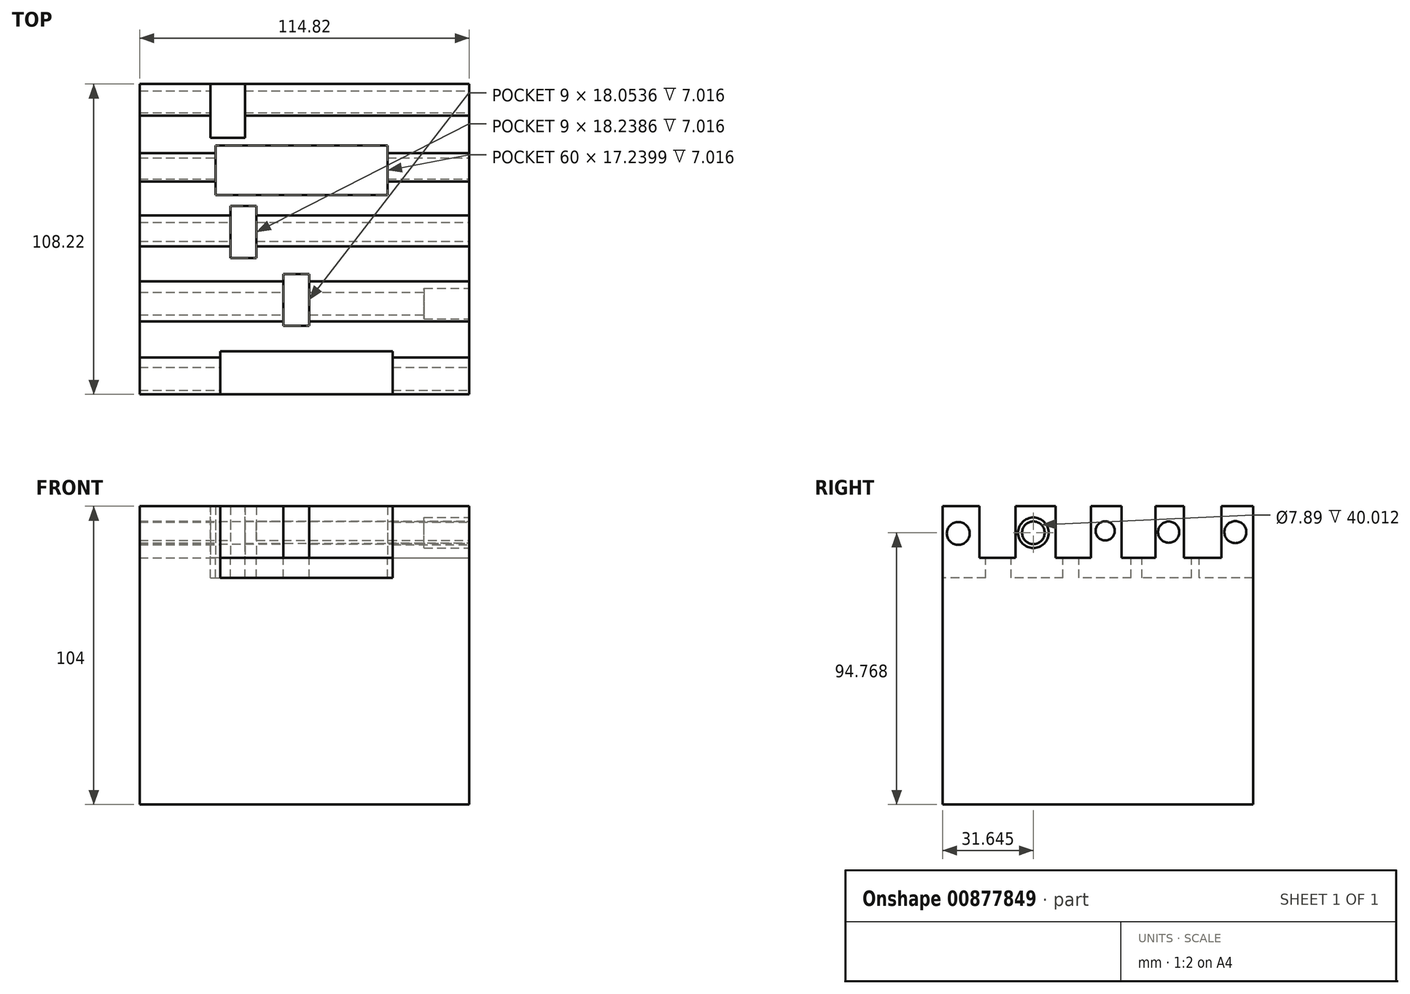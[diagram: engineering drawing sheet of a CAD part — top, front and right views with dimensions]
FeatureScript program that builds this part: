
annotation { "Feature Type Name" : "Feature", "Feature Type Description" : "" }
export const myFeature = defineFeature(function(context is Context, id is Id, definition is map)
    precondition{}
    {
        {
            var Q0;
            Q0=qCreatedBy(makeId("Top.planeOp"),FACE);
            var sketch = newSketch(context, id + "F0", { "sketchPlane" : qUnion([Q0])});
            skLineSegment(sketch, "E0.bottom", {"start": v(-43.96, -51.67) * mm, "end": v(70.86, -51.67) * mm});
            skLineSegment(sketch, "E0.top", {"start": v(-43.96, 56.55) * mm, "end": v(70.86, 56.55) * mm});
            skLineSegment(sketch, "E0.left", {"start": v(-43.96, -51.67) * mm, "end": v(-43.96, 56.55) * mm});
            skLineSegment(sketch, "E0.right", {"start": v(70.86, -51.67) * mm, "end": v(70.86, 56.55) * mm});
            skSolve(sketch);
        }
        {
            var Q0;
            Q0 = qSketchRegion(id + "F0", true);
            extrude(context, id + "F1", {"entities" : qUnion([Q0]), "depth" : 104 * mm, "offsetDistance" : 25 * mm});
        }
        {
            var Q0;
            Q0=makeQuery(id+"F1.opExtrude","SWEPT_FACE",FACE,{"disambiguationData":[OSD([sQuery(id+"F0.wireOp",EDGE,"E0.right")])]});
            var sketch = newSketch(context, id + "F2", { "sketchPlane" : qUnion([Q0])});
            skLineSegment(sketch, "E1.bottom", {"start": v(-38.8, 106.76) * mm, "end": v(-26.27, 106.76) * mm});
            skLineSegment(sketch, "E1.top", {"start": v(-38.8, 86.02) * mm, "end": v(-26.27, 86.02) * mm});
            skLineSegment(sketch, "E1.left", {"start": v(-38.8, 106.76) * mm, "end": v(-38.8, 86.02) * mm});
            skLineSegment(sketch, "E1.right", {"start": v(-26.27, 106.76) * mm, "end": v(-26.27, 86.02) * mm});
            skLineSegment(sketch, "E2.bottom", {"start": v(-12.25, 106.58) * mm, "end": v(0, 106.58) * mm});
            skLineSegment(sketch, "E2.top", {"start": v(-12.25, 86.02) * mm, "end": v(0, 86.02) * mm});
            skLineSegment(sketch, "E2.left", {"start": v(-12.25, 106.58) * mm, "end": v(-12.25, 86.02) * mm});
            skLineSegment(sketch, "E2.right", {"start": v(0, 106.58) * mm, "end": v(0, 86.02) * mm});
            skLineSegment(sketch, "E3.bottom", {"start": v(10.74, 106.76) * mm, "end": v(22.52, 106.76) * mm});
            skLineSegment(sketch, "E3.top", {"start": v(10.74, 86.02) * mm, "end": v(22.52, 86.02) * mm});
            skLineSegment(sketch, "E3.left", {"start": v(10.74, 106.76) * mm, "end": v(10.74, 86.02) * mm});
            skLineSegment(sketch, "E3.right", {"start": v(22.52, 106.76) * mm, "end": v(22.52, 86.02) * mm});
            skLineSegment(sketch, "E4.bottom", {"start": v(32.43, 106.58) * mm, "end": v(45.51, 106.58) * mm});
            skLineSegment(sketch, "E4.top", {"start": v(32.43, 86.02) * mm, "end": v(45.51, 86.02) * mm});
            skLineSegment(sketch, "E4.left", {"start": v(32.43, 106.58) * mm, "end": v(32.43, 86.02) * mm});
            skLineSegment(sketch, "E4.right", {"start": v(45.51, 106.58) * mm, "end": v(45.51, 86.02) * mm});
            skSolve(sketch);
        }
        {
            var Q0;
            Q0 = qSketchRegion(id + "F2", true);
            extrude(context, id + "F3", {"entities" : qUnion([Q0]), "operationType" : NewBodyOperationType.REMOVE, "endBound" : BoundingType.THROUGH_ALL, "oppositeDirection" : true, "depth" : 25 * mm, "offsetDistance" : 25 * mm});
        }
        {
            var Q0;
            {var subQ0=sQuery(id+"F0.wireOp",EDGE,"E0.bottom");var subQ1=sQuery(id+"F0.wireOp",EDGE,"E0.right");var subQ2=sQuery(id+"F0.wireOp",EDGE,"E0.left");Q0=makeQuery(id+"F3.boolean.opBoolean","SPLIT",FACE,{"disambiguationData":[TD([makeQuery(id+"F1.opExtrude","SWEPT_FACE",FACE,{"disambiguationData":[OSD([subQ0])]})])],"derivedFrom":makeQuery(id+"F1.opExtrude","CAP_FACE",FACE,{"disambiguationData":[OSD([subQ0,sQuery(id+"F0.wireOp",EDGE,"E0.top"),subQ2,subQ1])],"isStart":false})});}
            var sketch = newSketch(context, id + "F4", { "sketchPlane" : qUnion([Q0])});
            skLineSegment(sketch, "E5.bottom", {"start": v(-15.85, -36.65) * mm, "end": v(44.15, -36.65) * mm});
            skLineSegment(sketch, "E5.top", {"start": v(-15.85, -53.69) * mm, "end": v(44.15, -53.69) * mm});
            skLineSegment(sketch, "E5.left", {"start": v(-15.85, -36.65) * mm, "end": v(-15.85, -53.69) * mm});
            skLineSegment(sketch, "E5.right", {"start": v(44.15, -36.65) * mm, "end": v(44.15, -53.69) * mm});
            skLineSegment(sketch, "E6.bottom", {"start": v(6.15, -9.7) * mm, "end": v(15.15, -9.7) * mm});
            skLineSegment(sketch, "E6.top", {"start": v(6.15, -27.75) * mm, "end": v(15.15, -27.75) * mm});
            skLineSegment(sketch, "E6.left", {"start": v(6.15, -9.7) * mm, "end": v(6.15, -27.75) * mm});
            skLineSegment(sketch, "E6.right", {"start": v(15.15, -9.7) * mm, "end": v(15.15, -27.75) * mm});
            skLineSegment(sketch, "E7.bottom", {"start": v(-12.27, 14.08) * mm, "end": v(-3.27, 14.08) * mm});
            skLineSegment(sketch, "E7.top", {"start": v(-12.27, -4.16) * mm, "end": v(-3.27, -4.16) * mm});
            skLineSegment(sketch, "E7.left", {"start": v(-12.27, 14.08) * mm, "end": v(-12.27, -4.16) * mm});
            skLineSegment(sketch, "E7.right", {"start": v(-3.27, 14.08) * mm, "end": v(-3.27, -4.16) * mm});
            skLineSegment(sketch, "E8.bottom", {"start": v(-17.55, 35.07) * mm, "end": v(42.45, 35.07) * mm});
            skLineSegment(sketch, "E8.top", {"start": v(-17.55, 17.83) * mm, "end": v(42.45, 17.83) * mm});
            skLineSegment(sketch, "E8.left", {"start": v(-17.55, 35.07) * mm, "end": v(-17.55, 17.83) * mm});
            skLineSegment(sketch, "E8.right", {"start": v(42.45, 35.07) * mm, "end": v(42.45, 17.83) * mm});
            skLineSegment(sketch, "E9.bottom", {"start": v(-19.26, 60.98) * mm, "end": v(-7.26, 60.98) * mm});
            skLineSegment(sketch, "E9.top", {"start": v(-19.26, 37.77) * mm, "end": v(-7.26, 37.77) * mm});
            skLineSegment(sketch, "E9.left", {"start": v(-19.26, 60.98) * mm, "end": v(-19.26, 37.77) * mm});
            skLineSegment(sketch, "E9.right", {"start": v(-7.26, 60.98) * mm, "end": v(-7.26, 37.77) * mm});
            skSolve(sketch);
        }
        {
            var Q0;
            Q0 = qSketchRegion(id + "F4", true);
            var Q1;
            {var subQ0=sQuery(id+"F0.wireOp",EDGE,"E0.left");var subQ1=sQuery(id+"F0.wireOp",EDGE,"E0.right");Q1=makeQuery(id+"F3.boolean.opBoolean","SPLIT",FACE,{"disambiguationData":[TD([makeQuery(id+"F3.opExtrude","SWEPT_FACE",FACE,{"disambiguationData":[OSD([sQuery(id+"F2.wireOp",EDGE,"E3.right")])]})])],"derivedFrom":makeQuery(id+"F1.opExtrude","CAP_FACE",FACE,{"disambiguationData":[OSD([sQuery(id+"F0.wireOp",EDGE,"E0.bottom"),sQuery(id+"F0.wireOp",EDGE,"E0.top"),subQ0,subQ1])],"isStart":false})});}
            extrude(context, id + "F5", {"entities" : qUnion([Q0]), "operationType" : NewBodyOperationType.REMOVE, "oppositeDirection" : true, "depth" : 25 * mm, "endBoundEntityFace" : qUnion([Q1]), "offsetDistance" : 25 * mm});
        }
        {
            var Q0;
            Q0=makeQuery(id+"F1.opExtrude","SWEPT_FACE",FACE,{"disambiguationData":[OSD([sQuery(id+"F0.wireOp",EDGE,"E0.right")])]});
            var sketch = newSketch(context, id + "F6", { "sketchPlane" : qUnion([Q0])});
            skCircle(sketch, "E10", {"center": v(-46.2, 94.54) * mm, "radius": 4 * mm});
            skCircle(sketch, "E11", {"center": v(-20.02, 94.77) * mm, "radius": 3.95 * mm});
            skCircle(sketch, "E12", {"center": v(5.02, 95.44) * mm, "radius": 3.33 * mm});
            skCircle(sketch, "E13", {"center": v(50.37, 95) * mm, "radius": 3.84 * mm});
            skCircle(sketch, "E14", {"center": v(27.13, 95) * mm, "radius": 3.7 * mm});
            skSolve(sketch);
        }
        {
            var Q0;
            Q0 = qSketchRegion(id + "F6", true);
            extrude(context, id + "F7", {"entities" : qUnion([Q0]), "operationType" : NewBodyOperationType.REMOVE, "endBound" : BoundingType.THROUGH_ALL, "oppositeDirection" : true, "depth" : 25 * mm, "offsetDistance" : 25 * mm});
        }
        {
            var Q0;
            Q0=makeQuery(id+"F1.opExtrude","SWEPT_FACE",FACE,{"disambiguationData":[OSD([sQuery(id+"F0.wireOp",EDGE,"E0.right")])]});
            var sketch = newSketch(context, id + "F8", { "sketchPlane" : qUnion([Q0])});
            skCircle(sketch, "E15", {"center": v(-20.02, 94.77) * mm, "radius": 5.32 * mm});
            skSolve(sketch);
        }
        {
            var Q0;
            Q0 = qSketchRegion(id + "F8", true);
            extrude(context, id + "F9", {"entities" : qUnion([Q0]), "operationType" : NewBodyOperationType.REMOVE, "oppositeDirection" : true, "depth" : 15.7 * mm, "offsetDistance" : 25 * mm});
        }
    });
